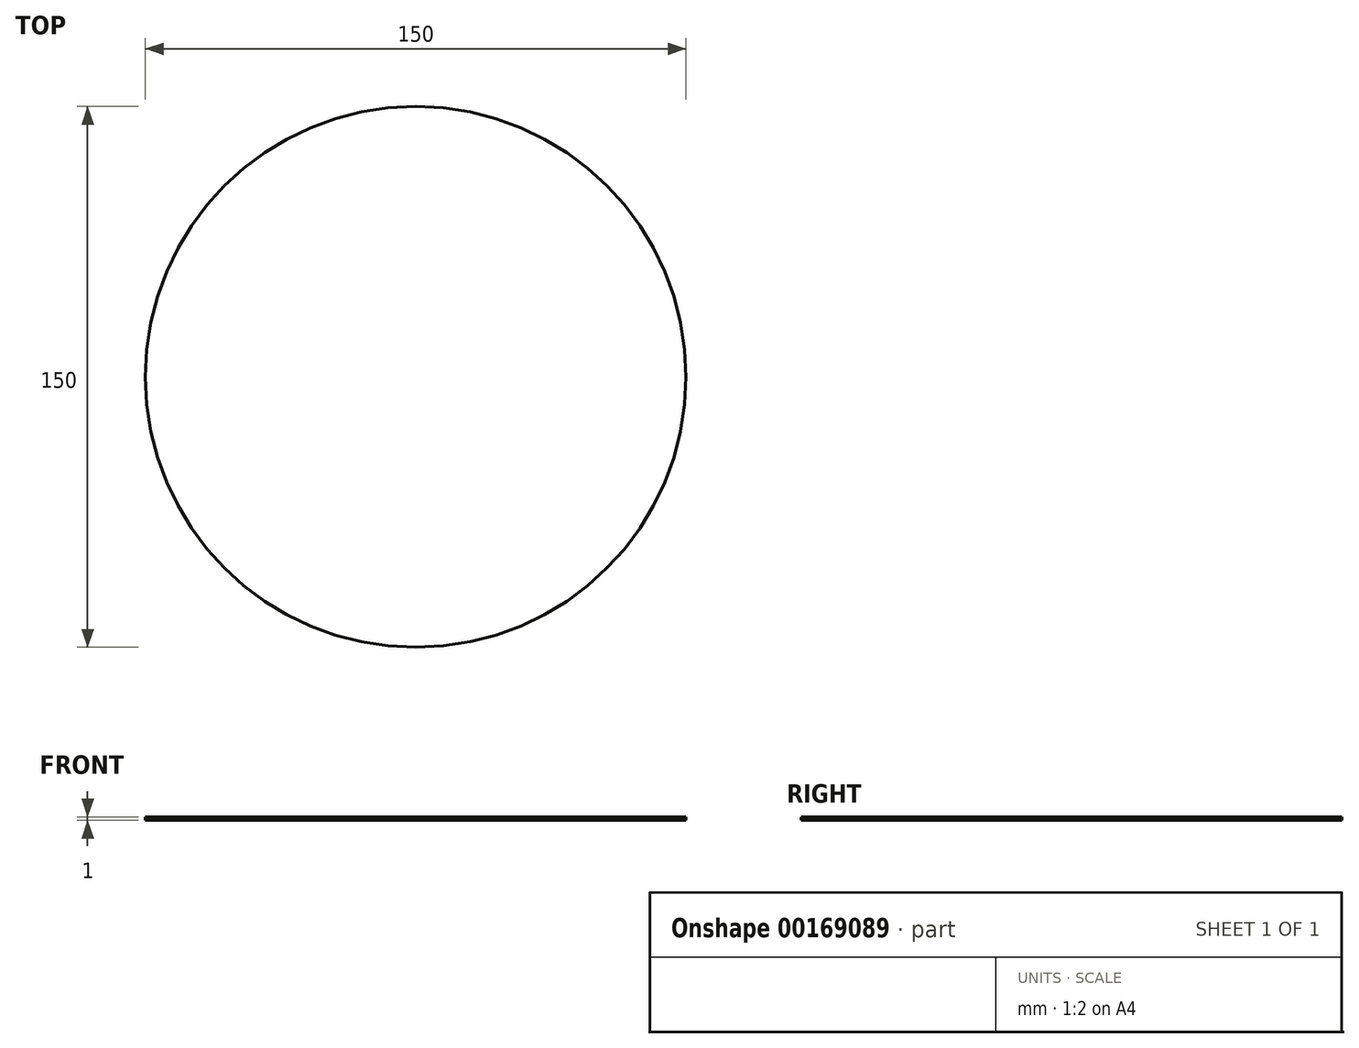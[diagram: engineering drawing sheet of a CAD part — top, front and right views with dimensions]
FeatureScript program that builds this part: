
annotation { "Feature Type Name" : "Feature", "Feature Type Description" : "" }
export const myFeature = defineFeature(function(context is Context, id is Id, definition is map)
    precondition{}
    {
        {
            var Q0;
            Q0=qCreatedBy(makeId("Top.planeOp"),FACE);
            var sketch = newSketch(context, id + "F0", { "sketchPlane" : qUnion([Q0])});
            skCircle(sketch, "E0", {"center": v(0, 0) * mm, "radius": 75 * mm});
            skSolve(sketch);
        }
        {
            var Q0;
            Q0 = qSketchRegion(id + "F0", true);
            extrude(context, id + "F1", {"entities" : qUnion([Q0]), "depth" : 1 * mm});
        }
    });
